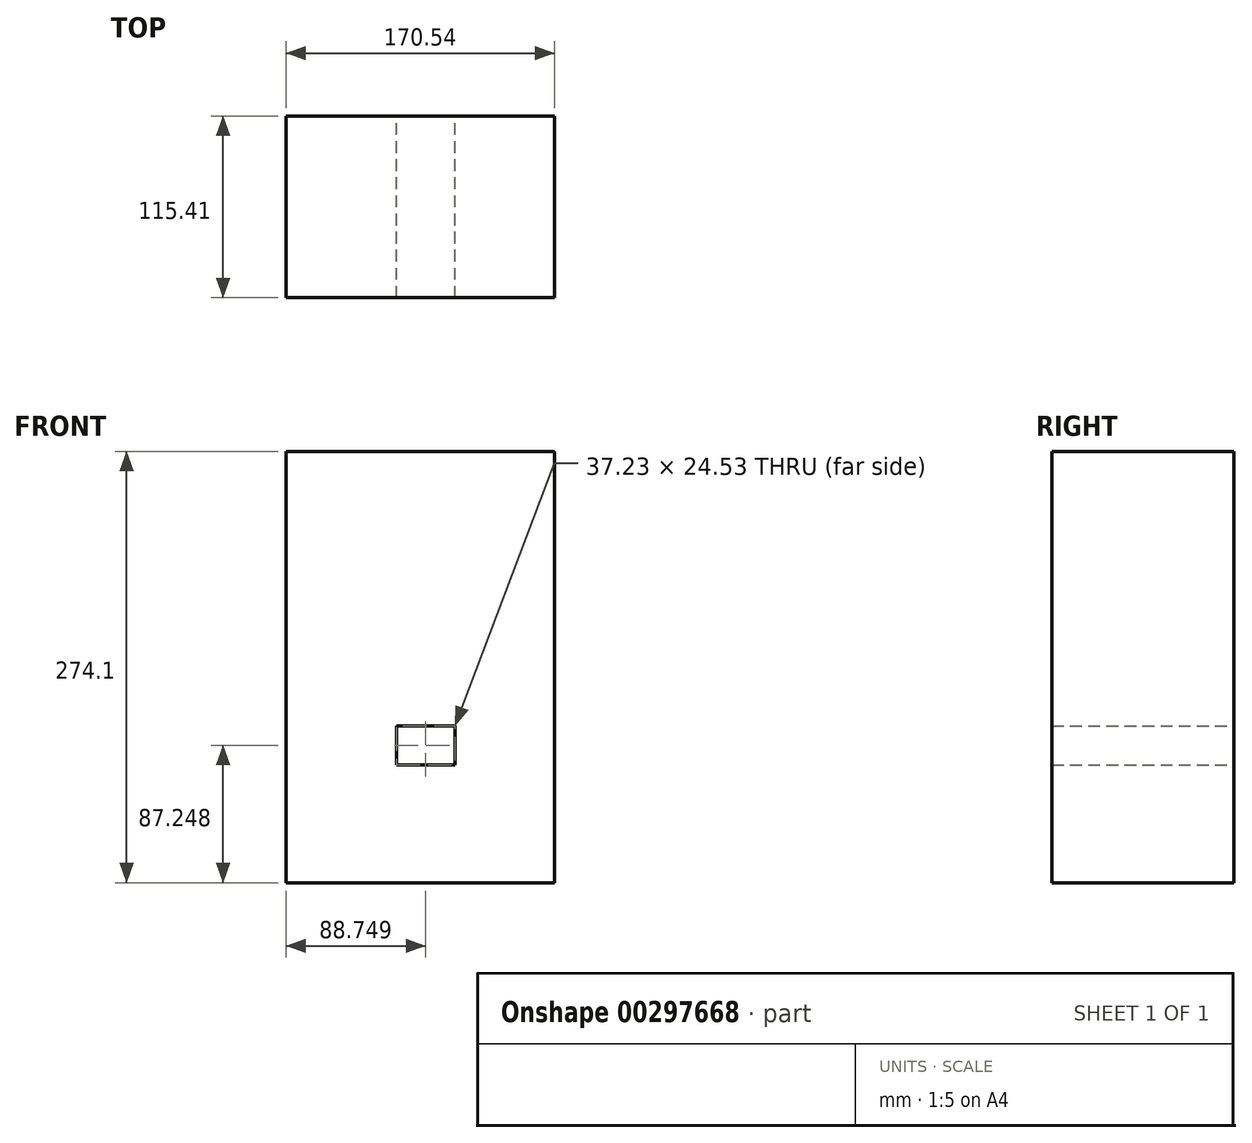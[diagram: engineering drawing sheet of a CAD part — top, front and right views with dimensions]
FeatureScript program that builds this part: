
annotation { "Feature Type Name" : "Feature", "Feature Type Description" : "" }
export const myFeature = defineFeature(function(context is Context, id is Id, definition is map)
    precondition{}
    {
        {
            var Q0;
            Q0=qCreatedBy(makeId("Front.planeOp"),FACE);
            var sketch = newSketch(context, id + "F0", { "sketchPlane" : qUnion([Q0])});
            skLineSegment(sketch, "E0.bottom", {"start": v(-88.2, 50.9) * mm, "end": v(82.34, 50.9) * mm});
            skLineSegment(sketch, "E0.top", {"start": v(-88.2, -223.2) * mm, "end": v(82.34, -223.2) * mm});
            skLineSegment(sketch, "E0.left", {"start": v(-88.2, 50.9) * mm, "end": v(-88.2, -223.2) * mm});
            skLineSegment(sketch, "E0.right", {"start": v(82.34, 50.9) * mm, "end": v(82.34, -223.2) * mm});
            skLineSegment(sketch, "E1.bottom", {"start": v(19.17, -123.7) * mm, "end": v(-18.07, -123.7) * mm});
            skLineSegment(sketch, "E1.top", {"start": v(19.17, -148.23) * mm, "end": v(-18.07, -148.23) * mm});
            skLineSegment(sketch, "E1.left", {"start": v(19.17, -123.7) * mm, "end": v(19.17, -148.23) * mm});
            skLineSegment(sketch, "E1.right", {"start": v(-18.07, -123.7) * mm, "end": v(-18.07, -148.23) * mm});
            skSolve(sketch);
        }
        {
            var Q0;
            Q0=makeQuery(id+"F0.imprint","IMPRINT",FACE,{"disambiguationData":[TD([[makeQuery(id+"F0.imprint","IMPRINT",EDGE,{"derivedFrom":sQuery(id+"F0.wireOp",EDGE,"E0.bottom")}),-1.0]])]});
            extrude(context, id + "F1", {"entities" : qUnion([Q0]), "depth" : 115.4 * mm, "offsetDistance" : 25 * mm});
        }
    });
